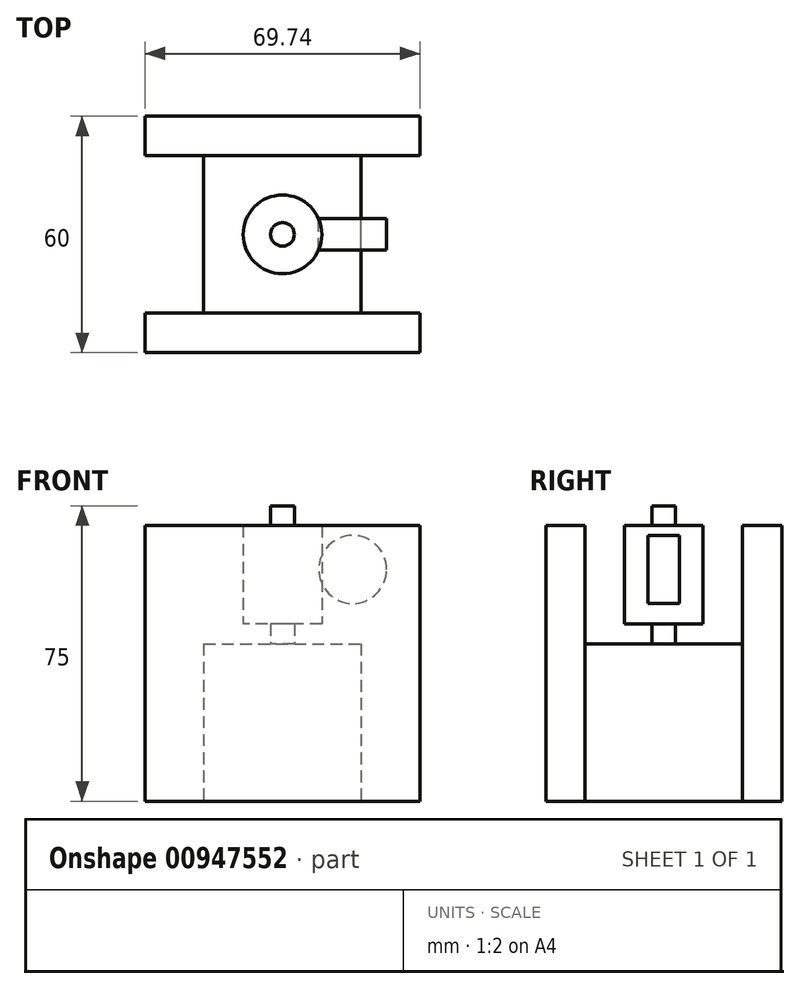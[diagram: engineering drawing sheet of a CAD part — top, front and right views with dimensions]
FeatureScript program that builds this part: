
annotation { "Feature Type Name" : "Feature", "Feature Type Description" : "" }
export const myFeature = defineFeature(function(context is Context, id is Id, definition is map)
    precondition{}
    {
        {
            var Q0;
            Q0=qCreatedBy(makeId("Top.planeOp"),FACE);
            var sketch = newSketch(context, id + "F0", { "sketchPlane" : qUnion([Q0])});
            skLineSegment(sketch, "E0.bottom", {"start": v(-20, -20) * mm, "end": v(20, -20) * mm});
            skLineSegment(sketch, "E0.top", {"start": v(-20, 20) * mm, "end": v(20, 20) * mm});
            skLineSegment(sketch, "E0.left", {"start": v(-20, -20) * mm, "end": v(-20, 20) * mm});
            skLineSegment(sketch, "E0.right", {"start": v(20, -20) * mm, "end": v(20, 20) * mm});
            skLineSegment(sketch, "E1", {"start": v(0, 0) * mm, "end": v(0, -20) * mm, "construction": true});
            skLineSegment(sketch, "E2", {"start": v(0, 0) * mm, "end": v(20, 0) * mm, "construction": true});
            skSolve(sketch);
        }
        {
            var Q0;
            Q0=makeQuery(id+"F0.imprint","IMPRINT",FACE,{"disambiguationData":[TD([[makeQuery(id+"F0.imprint","IMPRINT",EDGE,{"derivedFrom":sQuery(id+"F0.wireOp",EDGE,"E0.bottom")}),1.0]])]});
            extrude(context, id + "F1", {"entities" : qUnion([Q0]), "depth" : 40 * mm, "offsetDistance" : 25 * mm});
        }
        {
            var Q0;
            Q0=makeQuery(id+"F1.opExtrude","CAP_FACE",FACE,{"disambiguationData":[OSD([sQuery(id+"F0.wireOp",EDGE,"E0.bottom"),sQuery(id+"F0.wireOp",EDGE,"E0.top"),sQuery(id+"F0.wireOp",EDGE,"E0.left"),sQuery(id+"F0.wireOp",EDGE,"E0.right")])],"isStart":false});
            var sketch = newSketch(context, id + "F2", { "sketchPlane" : qUnion([Q0])});
            skLineSegment(sketch, "E3", {"start": v(20, 0) * mm, "end": v(0, 0) * mm, "construction": true});
            skLineSegment(sketch, "E4", {"start": v(0, 0) * mm, "end": v(0, -20) * mm, "construction": true});
            skCircle(sketch, "E5", {"center": v(0, 0) * mm, "radius": 3 * mm});
            skSolve(sketch);
        }
        {
            var Q0;
            Q0=makeQuery(id+"F2.imprint","IMPRINT",FACE,{"disambiguationData":[TD([[makeQuery(id+"F2.imprint","IMPRINT",EDGE,{"derivedFrom":sQuery(id+"F2.wireOp",EDGE,"E5")}),1.0]])]});
            var Q1;
            Q1=sQuery(id+"F2.wireOp",EDGE,"E5");
            extrude(context, id + "F3", {"entities" : qUnion([Q0]), "surfaceEntities" : qUnion([Q1]), "depth" : 35 * mm, "offsetDistance" : 25 * mm});
        }
        {
            var Q0;
            Q0=makeQuery(id+"F1.opExtrude","CAP_FACE",FACE,{"disambiguationData":[OSD([sQuery(id+"F0.wireOp",EDGE,"E0.bottom"),sQuery(id+"F0.wireOp",EDGE,"E0.top"),sQuery(id+"F0.wireOp",EDGE,"E0.left"),sQuery(id+"F0.wireOp",EDGE,"E0.right")])],"isStart":false});
            cPlane(context, id + "F4", {"entities" : qUnion([Q0]), "cplaneType" : CPlaneType.OFFSET, "offset" : 5 * mm, "width" : 150 * mm, "height" : 150 * mm});
        }
        {
            var Q0;
            Q0=qCreatedBy(id+"F4.planeOp",FACE);
            var sketch = newSketch(context, id + "F5", { "sketchPlane" : qUnion([Q0])});
            skCircle(sketch, "E6", {"center": v(0, 0) * mm, "radius": 10 * mm});
            skSolve(sketch);
        }
        {
            var Q0;
            Q0=makeQuery(id+"F5.imprint","IMPRINT",FACE,{"disambiguationData":[TD([[makeQuery(id+"F5.imprint","IMPRINT",EDGE,{"derivedFrom":sQuery(id+"F5.wireOp",EDGE,"E6")}),1.0]])]});
            var Q1;
            Q1=sQuery(id+"F5.wireOp",EDGE,"E6");
            extrude(context, id + "F6", {"entities" : qUnion([Q0]), "operationType" : NewBodyOperationType.ADD, "surfaceEntities" : qUnion([Q1]), "depth" : 25 * mm, "offsetDistance" : 25 * mm});
        }
        {
            var Q0;
            Q0=qCreatedBy(makeId("Front.planeOp"),FACE);
            var sketch = newSketch(context, id + "F7", { "sketchPlane" : qUnion([Q0])});
            skCircle(sketch, "E7", {"center": v(17.83, 58.87) * mm, "radius": 8.62 * mm});
            skSolve(sketch);
        }
        {
            var Q0;
            Q0=makeQuery(id+"F7.imprint","IMPRINT",FACE,{"disambiguationData":[TD([[makeQuery(id+"F7.imprint","IMPRINT",EDGE,{"derivedFrom":sQuery(id+"F7.wireOp",EDGE,"E7")}),1.0]])]});
            var Q1;
            Q1=sQuery(id+"F7.wireOp",EDGE,"E7");
            extrude(context, id + "F8", {"entities" : qUnion([Q0]), "surfaceEntities" : qUnion([Q1]), "endBound" : BoundingType.SYMMETRIC, "depth" : 8 * mm, "offsetDistance" : 25 * mm});
        }
        {
            var Q0;
            Q0=qCreatedBy(makeId("Top.planeOp"),FACE);
            var sketch = newSketch(context, id + "F9", { "sketchPlane" : qUnion([Q0])});
            skLineSegment(sketch, "E8.bottom", {"start": v(34.87, 20) * mm, "end": v(-34.87, 20) * mm});
            skLineSegment(sketch, "E8.top", {"start": v(34.87, 30) * mm, "end": v(-34.87, 30) * mm});
            skLineSegment(sketch, "E8.left", {"start": v(34.87, 20) * mm, "end": v(34.87, 30) * mm});
            skLineSegment(sketch, "E8.right", {"start": v(-34.87, 20) * mm, "end": v(-34.87, 30) * mm});
            skLineSegment(sketch, "E9.bottom", {"start": v(-34.87, -20) * mm, "end": v(34.87, -20) * mm});
            skLineSegment(sketch, "E9.top", {"start": v(-34.87, -30) * mm, "end": v(34.87, -30) * mm});
            skLineSegment(sketch, "E9.left", {"start": v(-34.87, -20) * mm, "end": v(-34.87, -30) * mm});
            skLineSegment(sketch, "E9.right", {"start": v(34.87, -20) * mm, "end": v(34.87, -30) * mm});
            skSolve(sketch);
        }
        {
            var Q0;
            Q0=makeQuery(id+"F9.imprint","IMPRINT",FACE,{"disambiguationData":[TD([[makeQuery(id+"F9.imprint","IMPRINT",EDGE,{"derivedFrom":sQuery(id+"F9.wireOp",EDGE,"E8.bottom")}),-1.0]])]});
            var Q1;
            Q1=makeQuery(id+"F9.imprint","IMPRINT",FACE,{"disambiguationData":[TD([[makeQuery(id+"F9.imprint","IMPRINT",EDGE,{"derivedFrom":sQuery(id+"F9.wireOp",EDGE,"E9.bottom")}),-1.0]])]});
            extrude(context, id + "F10", {"entities" : qUnion([Q0, Q1]), "depth" : 70 * mm, "offsetDistance" : 25 * mm});
        }
        {
            var Q0;
            Q0=makeQuery(id+"F8.opExtrude","CAP_FACE",FACE,{"disambiguationData":[OSD([sQuery(id+"F7.wireOp",EDGE,"E7")])],"isStart":false});
            var sketch = newSketch(context, id + "F11", { "sketchPlane" : qUnion([Q0])});
            skCircle(sketch, "E10", {"center": v(17.83, 58.87) * mm, "radius": 2 * mm});
            skSolve(sketch);
        }
        {
            var Q0;
            Q0=sQuery(id+"F11.wireOp",EDGE,"E10");
            extrude(context, id + "F12", {"bodyType" : ToolBodyType.SURFACE, "surfaceEntities" : qUnion([Q0]), "endBound" : BoundingType.THROUGH_ALL, "depth" : 25 * mm, "offsetDistance" : 25 * mm, "hasSecondDirection" : true, "secondDirectionBound" : SecondDirectionBoundingType.THROUGH_ALL, "secondDirectionOppositeDirection" : true, "secondDirectionDepth" : 25 * mm});
        }
    });
